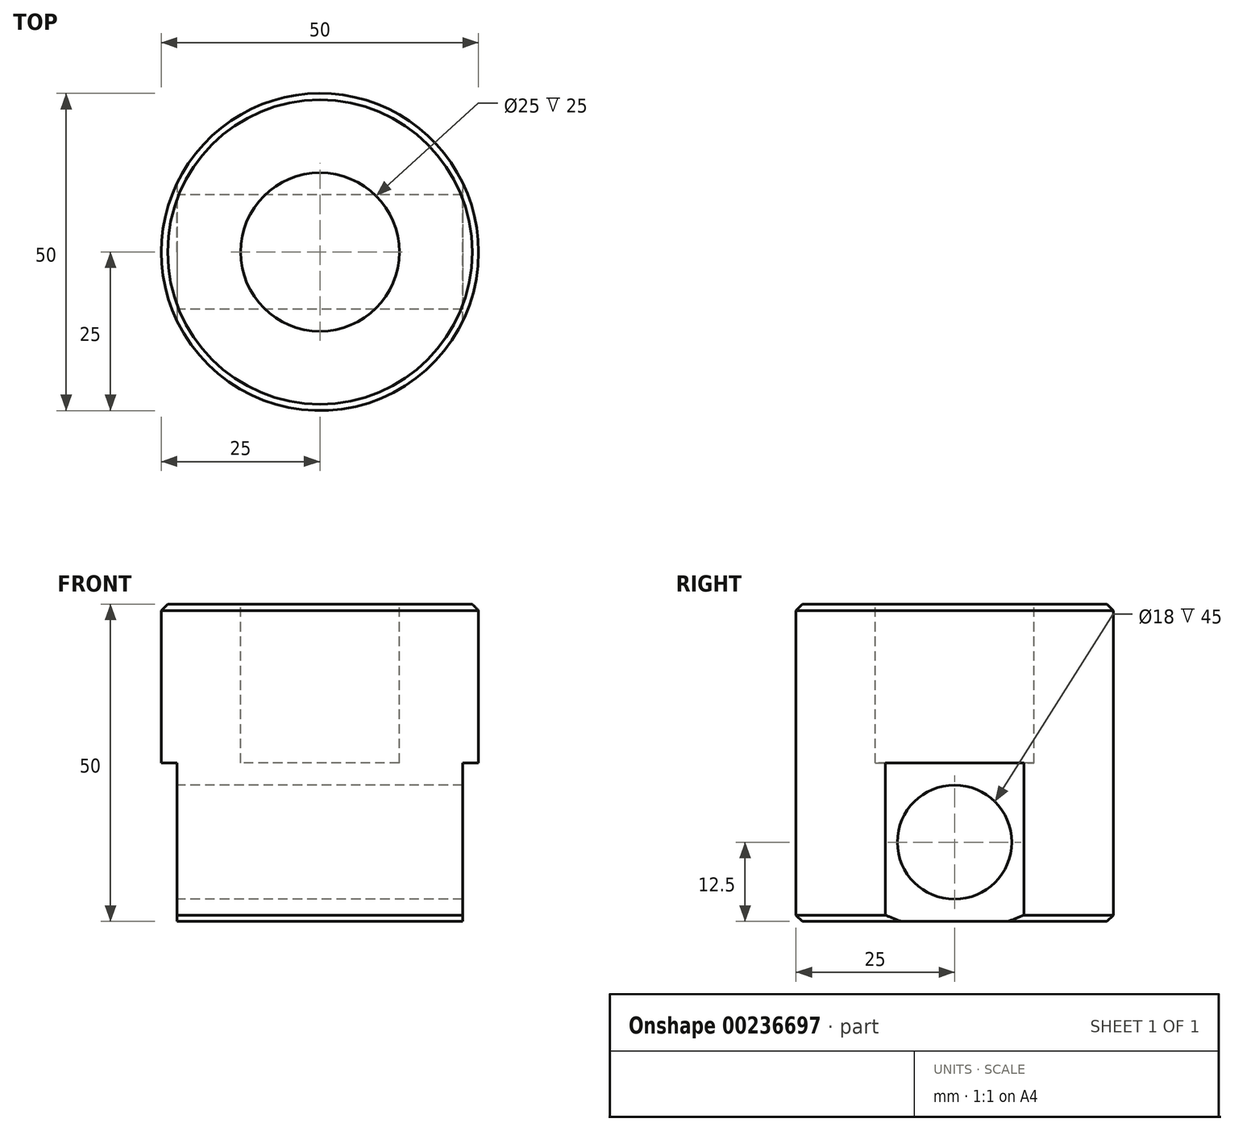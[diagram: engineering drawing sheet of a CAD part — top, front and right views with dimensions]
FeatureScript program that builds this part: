
annotation { "Feature Type Name" : "Feature", "Feature Type Description" : "" }
export const myFeature = defineFeature(function(context is Context, id is Id, definition is map)
    precondition{}
    {
        {
            var Q0;
            Q0=qCreatedBy(makeId("Top.planeOp"),FACE);
            var sketch = newSketch(context, id + "F0", { "sketchPlane" : qUnion([Q0])});
            skCircle(sketch, "E0", {"center": v(0, 0) * mm, "radius": 25 * mm});
            skSolve(sketch);
        }
        {
            var Q0;
            Q0=makeQuery(id+"F0.imprint","IMPRINT",FACE,{"disambiguationData":[TD([[makeQuery(id+"F0.imprint","IMPRINT",EDGE,{"derivedFrom":sQuery(id+"F0.wireOp",EDGE,"E0")}),1.0]])]});
            extrude(context, id + "F1", {"entities" : qUnion([Q0]), "depth" : 50 * mm});
        }
        {
            var Q0;
            Q0=qCreatedBy(makeId("Top.planeOp"),FACE);
            var sketch = newSketch(context, id + "F2", { "sketchPlane" : qUnion([Q0])});
            skLineSegment(sketch, "E1.bottom", {"start": v(22.5, 24.7) * mm, "end": v(46.25, 24.7) * mm});
            skLineSegment(sketch, "E1.top", {"start": v(22.5, -22.62) * mm, "end": v(46.25, -22.62) * mm});
            skLineSegment(sketch, "E1.left", {"start": v(22.5, 24.7) * mm, "end": v(22.5, -22.62) * mm});
            skLineSegment(sketch, "E1.right", {"start": v(46.25, 24.7) * mm, "end": v(46.25, -22.62) * mm});
            skLineSegment(sketch, "E2.bottom", {"start": v(-22.5, 24.7) * mm, "end": v(-36.61, 24.7) * mm});
            skLineSegment(sketch, "E2.top", {"start": v(-22.5, -22.62) * mm, "end": v(-36.61, -22.62) * mm});
            skLineSegment(sketch, "E2.left", {"start": v(-22.5, 24.7) * mm, "end": v(-22.5, -22.62) * mm});
            skLineSegment(sketch, "E2.right", {"start": v(-36.61, 24.7) * mm, "end": v(-36.61, -22.62) * mm});
            skSolve(sketch);
        }
        {
            var Q0;
            Q0 = qSketchRegion(id + "F2", true);
            extrude(context, id + "F3", {"entities" : qUnion([Q0]), "operationType" : NewBodyOperationType.REMOVE, "depth" : 25 * mm});
        }
        {
            var Q0;
            Q0=makeQuery(id+"F3.boolean.opBoolean","COPY",FACE,{"derivedFrom":makeQuery(id+"F3.opExtrude","SWEPT_FACE",FACE,{"disambiguationData":[OSD([sQuery(id+"F2.wireOp",EDGE,"E1.left")])]})});
            var sketch = newSketch(context, id + "F4", { "sketchPlane" : qUnion([Q0])});
            skPoint(sketch, "E3", {"position": v(0, 12.5) * mm});
            skSolve(sketch);
        }
        {
            var Q0;
            Q0=sQuery(id+"F4.wireOp",VERTEX,"E3");
            var Q1;
            Q1=makeQuery(id+"F1.opExtrude","SWEPT_BODY",BODY,{"disambiguationData":[OSD([sQuery(id+"F0.wireOp",EDGE,"E0")])]});
            hole(context, id + "F5", {"style" : HoleStyle.SIMPLE, "endStyle" : HoleEndStyle.THROUGH, "holeDiameter" : 18 * mm, "isTappedThrough" : true, "tappedDepth" : 12 * mm, "tapClearance" : 3, "locations" : qUnion([Q0]), "scope" : qUnion([Q1])});
        }
        {
            var Q0;
            Q0=makeQuery(id+"F1.opExtrude","CAP_FACE",FACE,{"disambiguationData":[OSD([sQuery(id+"F0.wireOp",EDGE,"E0")])],"isStart":false});
            var sketch = newSketch(context, id + "F6", { "sketchPlane" : qUnion([Q0])});
            skCircle(sketch, "E4", {"center": v(0, 0) * mm, "radius": 12.5 * mm});
            skSolve(sketch);
        }
        {
            var Q0;
            Q0 = qSketchRegion(id + "F6", true);
            extrude(context, id + "F7", {"entities" : qUnion([Q0]), "operationType" : NewBodyOperationType.REMOVE, "oppositeDirection" : true, "depth" : 25 * mm});
        }
        {
            var Q0;
            Q0=makeQuery(id+"F1.opExtrude","CAP_EDGE",EDGE,{"disambiguationData":[OSD([sQuery(id+"F0.wireOp",EDGE,"E0")])],"isStart":false});
            var Q1;
            Q1=makeQuery(id+"F3.boolean.opBoolean","SPLIT",EDGE,{"disambiguationData":[OD(1.0)],"derivedFrom":makeQuery(id+"F1.opExtrude","CAP_EDGE",EDGE,{"disambiguationData":[OSD([sQuery(id+"F0.wireOp",EDGE,"E0")])],"isStart":true})});
            var Q2;
            Q2=makeQuery(id+"F3.boolean.opBoolean","SPLIT",EDGE,{"disambiguationData":[OD(0.0)],"derivedFrom":makeQuery(id+"F1.opExtrude","CAP_EDGE",EDGE,{"disambiguationData":[OSD([sQuery(id+"F0.wireOp",EDGE,"E0")])],"isStart":true})});
            var Q3;
            Q3=makeQuery(id+"F3.boolean.opBoolean","COPY",EDGE,{"derivedFrom":makeQuery(id+"F3.opExtrude","CAP_EDGE",EDGE,{"disambiguationData":[OSD([sQuery(id+"F2.wireOp",EDGE,"E1.left")])],"isStart":true})});
            var Q4;
            Q4=makeQuery(id+"F3.boolean.opBoolean","COPY",EDGE,{"derivedFrom":makeQuery(id+"F3.opExtrude","CAP_EDGE",EDGE,{"disambiguationData":[OSD([sQuery(id+"F2.wireOp",EDGE,"E2.left")])],"isStart":true})});
            var Q5;
            Q5=makeQuery(id+"F5.hole-0.boolean.opBoolean","INTERSECT",EDGE,{"derivedFrom":[makeQuery(id+"F3.boolean.opBoolean","COPY",FACE,{"derivedFrom":makeQuery(id+"F3.opExtrude","SWEPT_FACE",FACE,{"disambiguationData":[OSD([sQuery(id+"F2.wireOp",EDGE,"E2.left")])]})}),makeQuery(id+"F5.hole-0.opRevolve","SWEPT_FACE",FACE,{"disambiguationData":[OSD([sQuery(id+"F5.hole-0.sketch.wireOp",EDGE,"core_line_2")])]})]});
            var Q6;
            Q6=makeQuery(id+"F7.boolean.opBoolean","COPY",EDGE,{"derivedFrom":makeQuery(id+"F7.opExtrude","CAP_EDGE",EDGE,{"disambiguationData":[OSD([sQuery(id+"F6.wireOp",EDGE,"E4")])],"isStart":true})});
            var Q7;
            Q7=makeQuery(id+"F5.hole-0.boolean.opBoolean","COPY",EDGE,{"derivedFrom":makeQuery(id+"F5.hole-0.opRevolve","SWEPT_EDGE",EDGE,{"disambiguationData":[OSD([sQuery(id+"F5.hole-0.sketch.wireOp",EDGE,"core_line_2"),sQuery(id+"F5.hole-0.sketch.wireOp",EDGE,"core_line_3")])]})});
            chamfer(context, id + "F8", {"entities" : qUnion([Q0, Q1, Q2, Q3, Q4, Q5, Q6, Q7]), "width" : 1 * mm, "tangentPropagation" : true});
        }
    });
